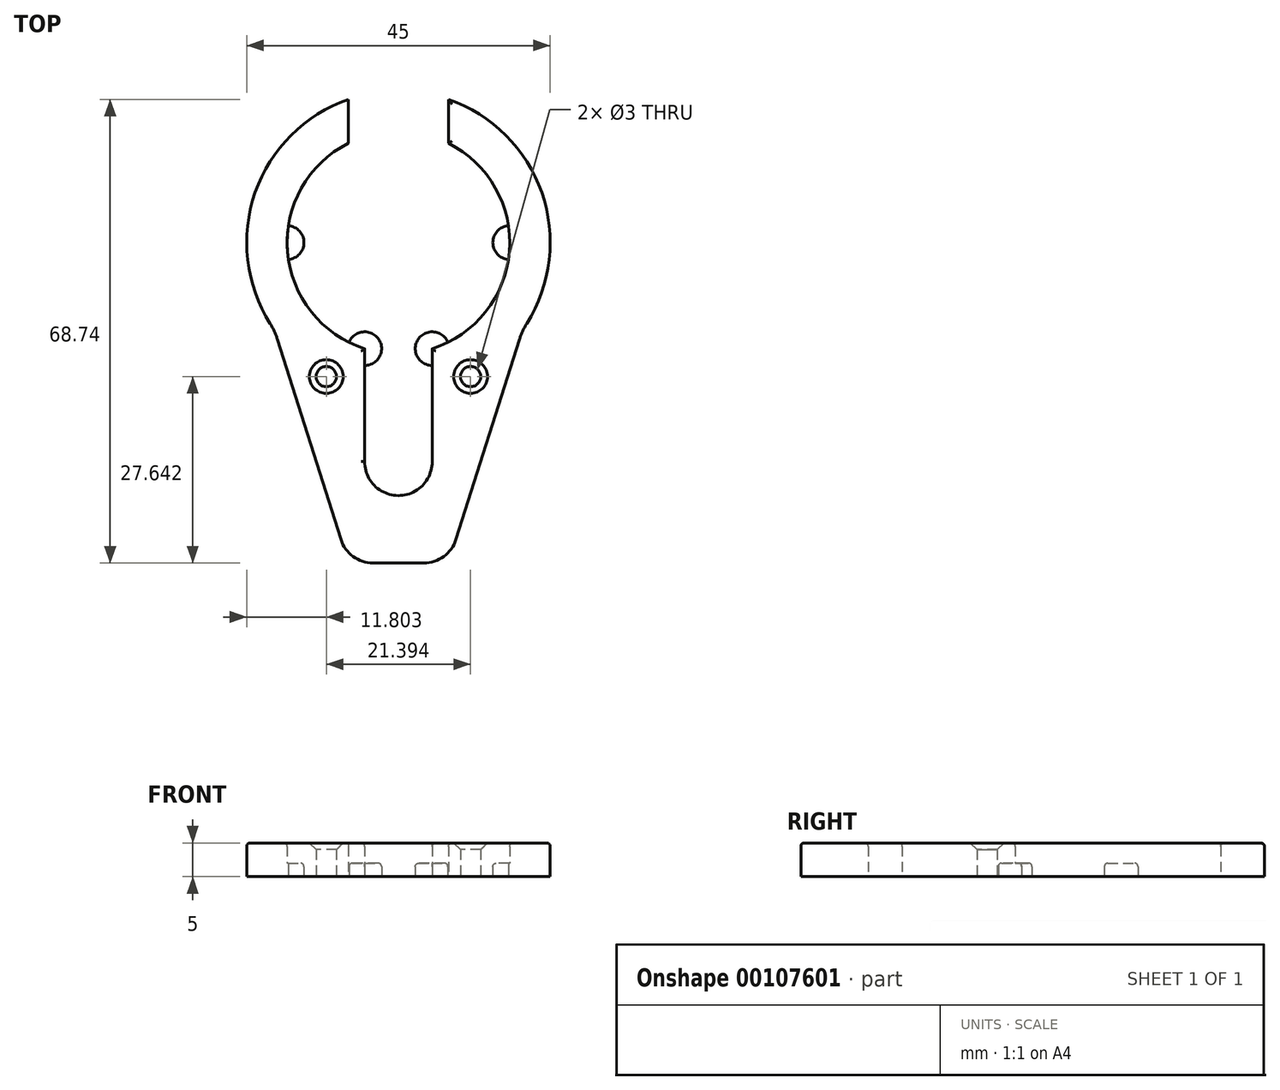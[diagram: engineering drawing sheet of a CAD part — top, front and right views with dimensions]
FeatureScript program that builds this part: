
annotation { "Feature Type Name" : "Feature", "Feature Type Description" : "" }
export const myFeature = defineFeature(function(context is Context, id is Id, definition is map)
    precondition{}
    {
        {
            var Q0;
            Q0=qCreatedBy(makeId("Top.planeOp"),FACE);
            var sketch = newSketch(context, id + "F0", { "sketchPlane" : qUnion([Q0])});
            skArc(sketch, "E0", {"start": v(-7.43, 14.73) * mm, "mid": v(-16.45, -1.31) * mm, "end": v(-5, -15.72) * mm});
            skArc(sketch, "E1", {"start": v(-7.43, 21.24) * mm, "mid": v(-21.24, 7.42) * mm, "end": v(-19.03, -12) * mm});
            skLineSegment(sketch, "E2.top", {"start": v(-3.77, -47.5) * mm, "end": v(3.77, -47.5) * mm});
            skLineSegment(sketch, "E2.left", {"start": v(-7.43, 21.24) * mm, "end": v(-7.43, 14.73) * mm});
            skLineSegment(sketch, "E2.right", {"start": v(7.43, 21.24) * mm, "end": v(7.43, 14.73) * mm});
            skArc(sketch, "E3", {"start": v(-16.31, -2.5) * mm, "mid": v(-14, 0) * mm, "end": v(-16.31, 2.5) * mm});
            skArc(sketch, "E4", {"start": v(16.31, 2.5) * mm, "mid": v(14, 0) * mm, "end": v(16.31, -2.5) * mm});
            skArc(sketch, "E5", {"start": v(-5, -32.45) * mm, "mid": v(-0.03, -37.5) * mm, "end": v(5, -32.5) * mm});
            skLineSegment(sketch, "E6", {"start": v(-5, -32.45) * mm, "end": v(-5, -15.72) * mm});
            skLineSegment(sketch, "E7", {"start": v(5, -32.5) * mm, "end": v(5, -15.72) * mm});
            skPoint(sketch, "E2.bottom.start.orphan", {"position": v(-7.43, 47.5) * mm});
            skPoint(sketch, "E8.orphan", {"position": v(7.43, 47.5) * mm});
            skArc(sketch, "E9.trimOffspring", {"start": v(5, -15.72) * mm, "mid": v(16.45, -1.31) * mm, "end": v(7.43, 14.73) * mm});
            skArc(sketch, "E10.trimOffspring", {"start": v(19.03, -12) * mm, "mid": v(21.24, 7.42) * mm, "end": v(7.43, 21.24) * mm});
            skLineSegment(sketch, "E11", {"start": v(-17.96, -14.31) * mm, "end": v(-8.53, -44.01) * mm});
            skLineSegment(sketch, "E12", {"start": v(17.96, -14.31) * mm, "end": v(8.53, -44.01) * mm});
            skPoint(sketch, "E13.orphan", {"position": v(-22.5, 0) * mm});
            skPoint(sketch, "E14.orphan", {"position": v(22.5, 0) * mm});
            skPoint(sketch, "E15.visualSharp", {"position": v(-7.43, -47.5) * mm});
            skArc(sketch, "E15.filletArc", {"start": v(-8.53, -44.01) * mm, "mid": v(-6.72, -46.53) * mm, "end": v(-3.77, -47.5) * mm});
            skPoint(sketch, "E16.visualSharp", {"position": v(7.43, -47.5) * mm});
            skArc(sketch, "E16.filletArc", {"start": v(3.77, -47.5) * mm, "mid": v(6.72, -46.53) * mm, "end": v(8.53, -44.01) * mm});
            skPoint(sketch, "E17.visualSharp", {"position": v(-18.38, -12.97) * mm});
            skArc(sketch, "E17.filletArc", {"start": v(-17.96, -14.31) * mm, "mid": v(-18.42, -13.12) * mm, "end": v(-19.03, -12) * mm});
            skPoint(sketch, "E18.visualSharp", {"position": v(18.38, -12.97) * mm});
            skArc(sketch, "E18.filletArc", {"start": v(19.03, -12) * mm, "mid": v(18.42, -13.12) * mm, "end": v(17.96, -14.31) * mm});
            skArc(sketch, "E19", {"start": v(-5, -18.22) * mm, "mid": v(-2.93, -14.33) * mm, "end": v(-7.32, -14.79) * mm});
            skArc(sketch, "E20", {"start": v(7.32, -14.79) * mm, "mid": v(2.93, -14.33) * mm, "end": v(5, -18.22) * mm});
            skPoint(sketch, "E21", {"position": v(0, -37.5) * mm});
            skCircle(sketch, "E22", {"center": v(-10.7, -19.86) * mm, "radius": 1.5 * mm});
            skLineSegment(sketch, "E23", {"start": v(0, 0) * mm, "end": v(0, -32.5) * mm, "construction": true});
            skCircle(sketch, "E24.MirrorC", {"center": v(10.7, -19.86) * mm, "radius": 1.5 * mm});
            skSolve(sketch);
        }
        {
            var Q0;
            Q0=makeQuery(id+"F0.imprint","IMPRINT",FACE,{"disambiguationData":[TD([[makeQuery(id+"F0.imprint","IMPRINT",EDGE,{"derivedFrom":sQuery(id+"F0.wireOp",EDGE,"E1")}),1.0]])]});
            extrude(context, id + "F1", {"entities" : qUnion([Q0]), "depth" : 5 * mm});
        }
        {
            var Q0;
            {var subQ0=sQuery(id+"F0.wireOp",EDGE,"E3");Q0=makeQuery(id+"F0.imprint","IMPRINT",FACE,{"disambiguationData":[TD([[makeQuery(id+"F0.imprint","IMPRINT",EDGE,{"derivedFrom":subQ0}),1.0]])]});}
            var Q1;
            {var subQ0=sQuery(id+"F0.wireOp",EDGE,"E4");Q1=makeQuery(id+"F0.imprint","IMPRINT",FACE,{"disambiguationData":[TD([[makeQuery(id+"F0.imprint","IMPRINT",EDGE,{"derivedFrom":subQ0}),1.0]])]});}
            var Q2;
            {var subQ3=sQuery(id+"F0.wireOp",EDGE,"E19");Q2=makeQuery(id+"F0.imprint","IMPRINT",FACE,{"disambiguationData":[TD([[makeQuery(id+"F0.imprint","IMPRINT",EDGE,{"derivedFrom":subQ3}),1.0]])]});}
            var Q3;
            {var subQ3=sQuery(id+"F0.wireOp",EDGE,"E20");Q3=makeQuery(id+"F0.imprint","IMPRINT",FACE,{"disambiguationData":[TD([[makeQuery(id+"F0.imprint","IMPRINT",EDGE,{"derivedFrom":subQ3}),1.0]])]});}
            extrude(context, id + "F2", {"entities" : qUnion([Q0, Q1, Q2, Q3]), "operationType" : NewBodyOperationType.ADD, "depth" : 2 * mm});
        }
        {
            var Q0;
            Q0=makeQuery(id+"F1.opExtrude","CAP_EDGE",EDGE,{"disambiguationData":[OSD([sQuery(id+"F0.wireOp",EDGE,"E1")])],"isStart":false});
            var Q1;
            Q1=makeQuery(id+"F1.opExtrude","CAP_EDGE",EDGE,{"disambiguationData":[OSD([sQuery(id+"F0.wireOp",EDGE,"E6")])],"isStart":false});
            var Q2;
            Q2=makeQuery(id+"F1.opExtrude","CAP_EDGE",EDGE,{"disambiguationData":[OSD([sQuery(id+"F0.wireOp",EDGE,"E7")])],"isStart":false});
            var Q3;
            Q3=makeQuery(id+"F2.opExtrude","CAP_EDGE",EDGE,{"disambiguationData":[OSD([sQuery(id+"F0.wireOp",EDGE,"E3")])],"isStart":false});
            var Q4;
            Q4=makeQuery(id+"F2.opExtrude","CAP_EDGE",EDGE,{"disambiguationData":[OSD([sQuery(id+"F0.wireOp",EDGE,"E4")])],"isStart":false});
            var Q5;
            Q5=makeQuery(id+"F1.opExtrude","CAP_EDGE",EDGE,{"disambiguationData":[OSD([sQuery(id+"F0.wireOp",EDGE,"E2.left")])],"isStart":false});
            var Q6;
            Q6=makeQuery(id+"F1.opExtrude","CAP_EDGE",EDGE,{"disambiguationData":[OSD([sQuery(id+"F0.wireOp",EDGE,"E2.right")])],"isStart":false});
            var Q7;
            Q7=makeQuery(id+"F2.opExtrude","CAP_EDGE",EDGE,{"disambiguationData":[OSD([sQuery(id+"F0.wireOp",EDGE,"E19")])],"isStart":false});
            var Q8;
            Q8=makeQuery(id+"F2.opExtrude","CAP_EDGE",EDGE,{"disambiguationData":[OSD([sQuery(id+"F0.wireOp",EDGE,"E20")])],"isStart":false});
            var Q9;
            Q9=makeQuery(id+"F1.opExtrude","CAP_EDGE",EDGE,{"disambiguationData":[OSD([sQuery(id+"F0.wireOp",EDGE,"E0")])],"isStart":false});
            var Q10;
            Q10=makeQuery(id+"F1.opExtrude","CAP_EDGE",EDGE,{"disambiguationData":[OSD([sQuery(id+"F0.wireOp",EDGE,"E9.trimOffspring")])],"isStart":false});
            fillet(context, id + "F3", {"entities" : qUnion([Q0, Q1, Q2, Q3, Q4, Q5, Q6, Q7, Q8, Q9, Q10]), "radius" : 0.5 * mm, "tangentPropagation" : true, "allowEdgeOverflow" : false});
        }
        {
            var Q0;
            Q0=makeQuery(id+"F1.opExtrude","CAP_EDGE",EDGE,{"disambiguationData":[OSD([sQuery(id+"F0.wireOp",EDGE,"E22")])],"isStart":false});
            var Q1;
            Q1=makeQuery(id+"F1.opExtrude","CAP_EDGE",EDGE,{"disambiguationData":[OSD([sQuery(id+"F0.wireOp",EDGE,"E24.MirrorC")])],"isStart":false});
            chamfer(context, id + "F4", {"entities" : qUnion([Q0, Q1]), "width" : 1 * mm, "tangentPropagation" : true});
        }
    });
